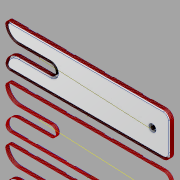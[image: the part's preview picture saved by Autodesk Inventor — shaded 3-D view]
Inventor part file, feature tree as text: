
AUTODESK INVENTOR PART (.ipt)
format: ipt  version: 2021.3 (Build 253353000, 353)  size: 177,152 bytes
history: native  units: in
note: dims shown in document units (in); Inventor stores cm internally (conversion verified against a paired STEP export)
features: other x7, sketch x3, extrude x2, fillet x2, reference x2, hole x1
ambient origin geometry x8: Origin, YZ Plane, XZ Plane, XY Plane, X Axis, Y Axis, Z Axis, Center Point
bodies: Body1 (feature_tree)
feature tree (17):
  other  "ソリッド1"
  other  "作業平面1"
  extrude  "押し出し1"  Depth=5.9055in
  extrude  "押し出し2"  Depth=0.7087in
  fillet  "フィレット1"  Radius=0.7087in
  other  "作業平面2"
  hole  "穴1"  [1 undecoded]
  fillet  "フィレット2"  Radius=0.1181in
  other  "作業平面3"
  sketch  "スケッチ2"
  reference  "参照5"
  sketch  "スケッチ3"
  reference  "参照6"
  sketch  "スケッチ4"
  other  "<userpath>\workspace\beetle_inventor_model\suspension\rocker.iam"
  other  "rocker.iam"
  other  "6inch_wheel:1"
note: 1 required parameter value undecoded (feature->parameter linkage not recoverable at this tier; creation-order binding heuristic only, values carry confidence <= 0.55)
